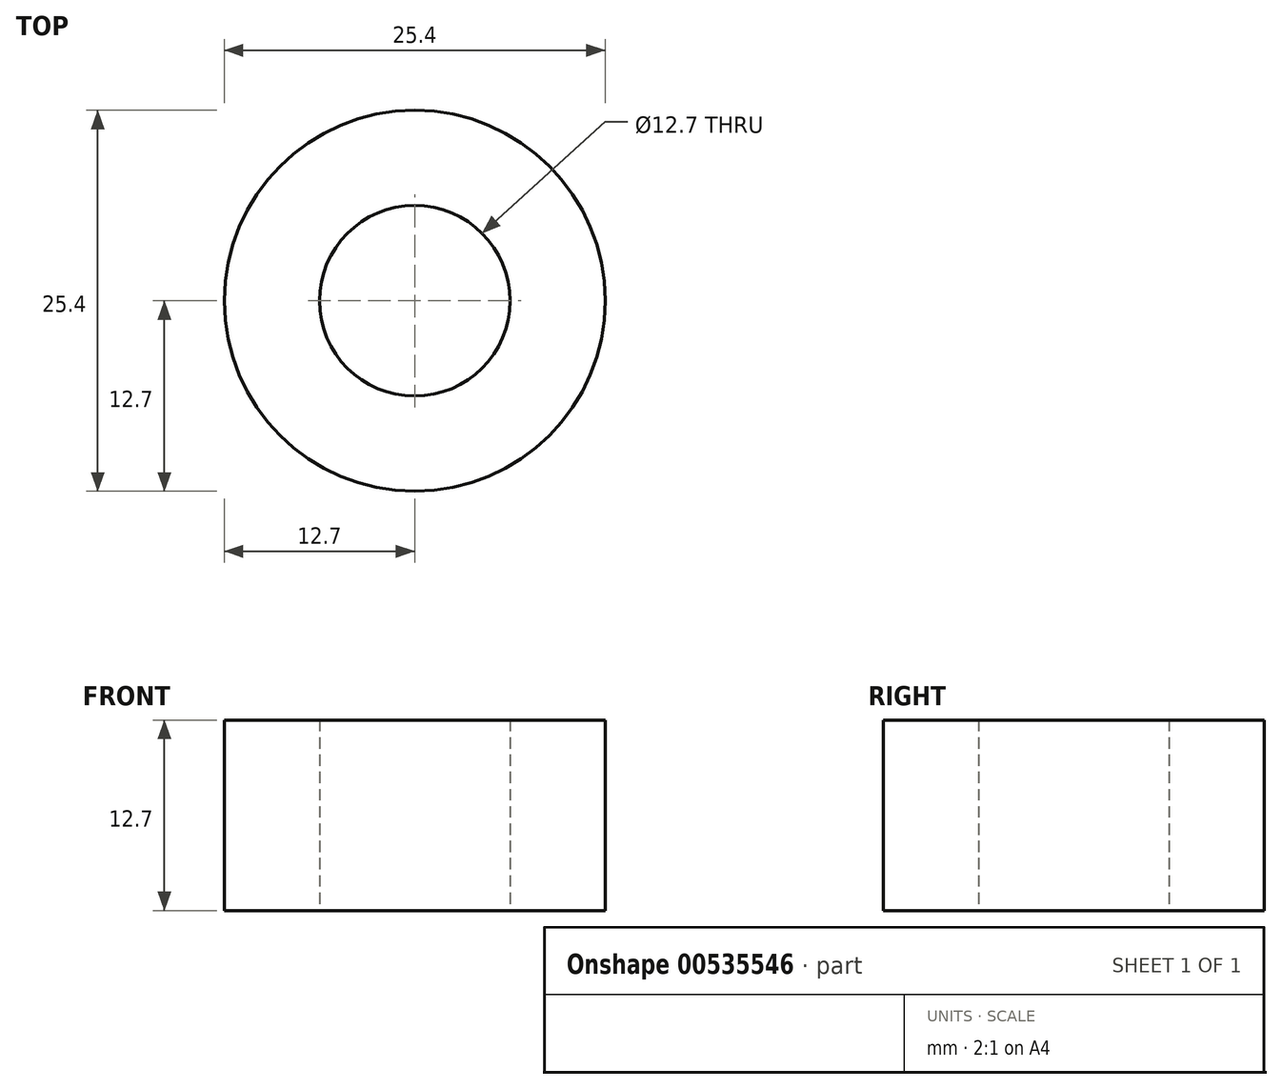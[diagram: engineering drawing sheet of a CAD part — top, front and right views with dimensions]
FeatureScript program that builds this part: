
annotation { "Feature Type Name" : "Feature", "Feature Type Description" : "" }
export const myFeature = defineFeature(function(context is Context, id is Id, definition is map)
    precondition{}
    {
        {
            var Q0;
            Q0=qCreatedBy(makeId("Top.planeOp"),FACE);
            var sketch = newSketch(context, id + "F0", { "sketchPlane" : qUnion([Q0])});
            skCircle(sketch, "E0", {"center": v(0, 0) * mm, "radius": 6.35 * mm});
            skCircle(sketch, "E1", {"center": v(0, 0) * mm, "radius": 12.7 * mm});
            skSolve(sketch);
        }
        {
            var Q0;
            Q0 = qSketchRegion(id + "F0", true);
            extrude(context, id + "F1", {"entities" : qUnion([Q0]), "depth" : 12.7 * mm, "offsetDistance" : 25 * mm});
        }
    });
